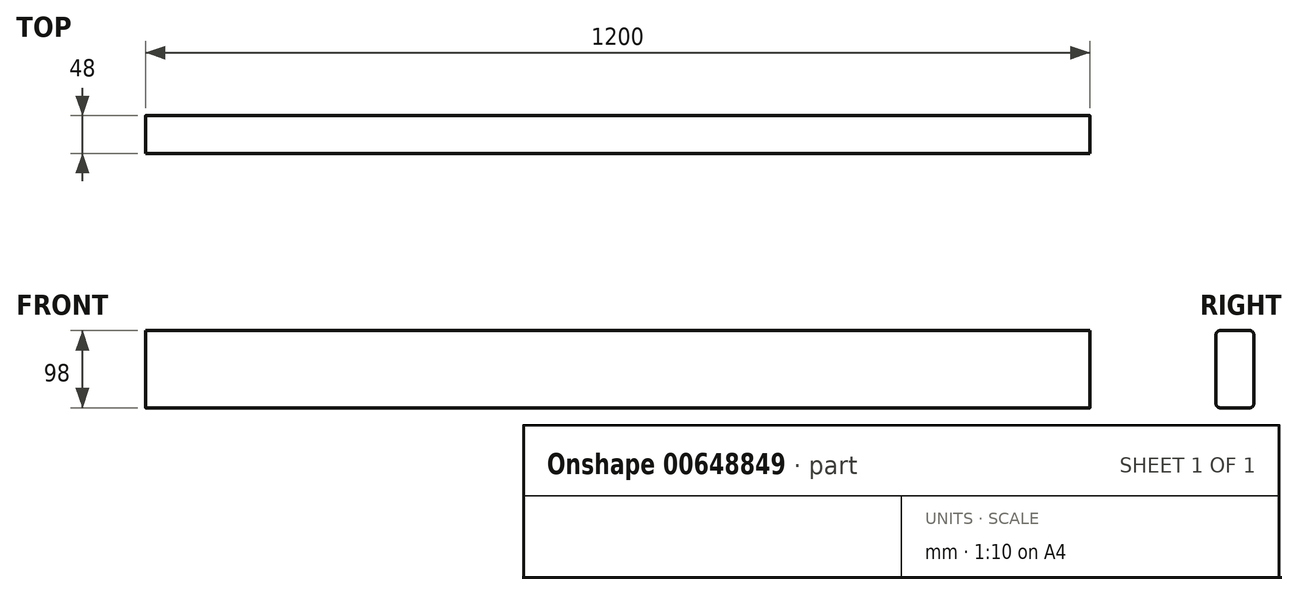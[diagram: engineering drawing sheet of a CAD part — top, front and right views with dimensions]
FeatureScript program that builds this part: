
annotation { "Feature Type Name" : "Feature", "Feature Type Description" : "" }
export const myFeature = defineFeature(function(context is Context, id is Id, definition is map)
    precondition{}
    {
        {
            var Q0;
            Q0=qCreatedBy(makeId("Top.planeOp"),FACE);
            var sketch = newSketch(context, id + "F0", { "sketchPlane" : qUnion([Q0])});
            skLineSegment(sketch, "E0.bottom", {"start": v(600, 24) * mm, "end": v(-600, 24) * mm});
            skLineSegment(sketch, "E0.top", {"start": v(600, -24) * mm, "end": v(-600, -24) * mm});
            skLineSegment(sketch, "E0.left", {"start": v(600, 24) * mm, "end": v(600, -24) * mm});
            skLineSegment(sketch, "E0.right", {"start": v(-600, 24) * mm, "end": v(-600, -24) * mm});
            skPoint(sketch, "E0.middle", {"position": v(0, 0) * mm});
            skSolve(sketch);
        }
        {
            var Q0;
            Q0=makeQuery(id+"F0.imprint","IMPRINT",FACE,{"disambiguationData":[TD([[makeQuery(id+"F0.imprint","IMPRINT",EDGE,{"derivedFrom":sQuery(id+"F0.wireOp",EDGE,"E0.bottom")}),1.0]])]});
            extrude(context, id + "F1", {"entities" : qUnion([Q0]), "endBound" : BoundingType.SYMMETRIC, "depth" : 98 * mm, "offsetDistance" : 25 * mm});
        }
        {
            var Q0;
            Q0=makeQuery(id+"F1.opExtrude","CAP_EDGE",EDGE,{"disambiguationData":[OSD([sQuery(id+"F0.wireOp",EDGE,"E0.top")])],"isStart":false});
            var Q1;
            Q1=makeQuery(id+"F1.opExtrude","CAP_EDGE",EDGE,{"disambiguationData":[OSD([sQuery(id+"F0.wireOp",EDGE,"E0.bottom")])],"isStart":false});
            var Q2;
            Q2=makeQuery(id+"F1.opExtrude","CAP_EDGE",EDGE,{"disambiguationData":[OSD([sQuery(id+"F0.wireOp",EDGE,"E0.top")])],"isStart":true});
            var Q3;
            Q3=makeQuery(id+"F1.opExtrude","CAP_EDGE",EDGE,{"disambiguationData":[OSD([sQuery(id+"F0.wireOp",EDGE,"E0.bottom")])],"isStart":true});
            fillet(context, id + "F2", {"entities" : qUnion([Q0, Q1, Q2, Q3]), "radius" : 5 * mm, "tangentPropagation" : true, "allowEdgeOverflow" : false});
        }
    });
